# Revit family: HermanMiller_Seating_Aeron_WorkChair
name_source: partatom
category: Furniture
revit_build: Autodesk Revit Architecture 2012 (Build: 20110622_0930(x64)
units: mm (PartAtom-declared; Revit-internal decimal feet)

## types (12) — shared parameters
Assembly Code = E2020200
Catalog = Seating (HST)
Manufacturer = Herman Miller, Inc.
Product Documentation Link = http://www.hermanmiller.com
Type Comments = Aeron Work Chair - AE11 Series
URL = http://www.hermanmiller.com

## per-type parameters (varying)
| type | Arm On | Armpad Finish | Base Finish | Description | Frame Finish | Lumbar Finish | Lumbar Support | Model | PostureFit Finish | PostureFit support | Seat Material |
| Arms No Back Support - Graphite Base/Graphite Frame | Yes | Herman Miller - Finish BK Black | Herman Miller - Finish G1 Graphite | Wk Chr Aeron Std-Ht Pneu Tlt Lim/Ang Ht Adj Arms NonuphstPds/B | Herman Miller - Finish G1 Graphite | Herman Miller - Finish BK Black | No | AE113HWB N2 G1 | Herman Miller - Finish G1 Graphite | No | Herman Miller - Pellicle 3D01 Classic Carbon |
| Arms No Back Support - Titanium Base/Smoke Frame | Yes | Herman Miller - Finish S8 Smoke | Herman Miller - Finish XT Titanium | Wk Chr Aeron Std-Ht Pneu Tlt Lim/Ang Ht Adj Arms NonuphstPds/B | Herman Miller - Finish S8 Smoke | Herman Miller - Finish S8 Smoke | No | AE113HWB N2 WS | Herman Miller - Finish S8 Smoke | No | Herman Miller - Pellicle 3V01 Classic Zinc |
| Arms Lumbar Support - Graphite Base/Graphite Frame | Yes | Herman Miller - Finish BK Black | Herman Miller - Finish G1 Graphite | Wk Chr Aeron Std-Ht Pneu Tlt Lim/Ang Ht Adj Arms NonuphstPds/B | Herman Miller - Finish G1 Graphite | Herman Miller - Finish BK Black | Yes | AE113HWB AJ G1 | Herman Miller - Finish G1 Graphite | No | Herman Miller - Pellicle 3D01 Classic Carbon |
| Arms Lumbar Support - Titanium Base/Smoke Frame | Yes | Herman Miller - Finish S8 Smoke | Herman Miller - Finish XT Titanium | Wk Chr Aeron Std-Ht Pneu Tlt Lim/Ang Ht Adj Arms NonuphstPds/B | Herman Miller - Finish S8 Smoke | Herman Miller - Finish S8 Smoke | Yes | AE113HWB AJ WS | Herman Miller - Finish S8 Smoke | No | Herman Miller - Pellicle 3V01 Classic Zinc |
| Arms PostureFit Support - Graphite Base/Graphite Frame | Yes | Herman Miller - Finish BK Black | Herman Miller - Finish G1 Graphite | Wk Chr Aeron Std-Ht Pneu Tlt Lim/Ang Ht Adj Arms NonuphstPds/B | Herman Miller - Finish G1 Graphite | Herman Miller - Finish BK Black | No | AE113HWB PJ G1 | Herman Miller - Finish G1 Graphite | Yes | Herman Miller - Pellicle 3D01 Classic Carbon |
| Arms PostureFit Support - Titanium Base/Smoke Frame | Yes | Herman Miller - Finish S8 Smoke | Herman Miller - Finish XT Titanium | Wk Chr Aeron Std-Ht Pneu Tlt Lim/Ang Ht Adj Arms NonuphstPds/B | Herman Miller - Finish S8 Smoke | Herman Miller - Finish S8 Smoke | No | AE113HWB PJ WS | Herman Miller - Finish S8 Smoke | Yes | Herman Miller - Pellicle 3V01 Classic Zinc |
| Without Arms No Back Support - Graphite Base/Graphite Frame | No | Herman Miller - Finish BK Black | Herman Miller - Finish G1 Graphite | Wk Chr Aeron Std-Ht Pneu. Tlt Lim/Ang No Arms/B | Herman Miller - Finish G1 Graphite | Herman Miller - Finish BK Black | No | AE113NNB N2 G1 | Herman Miller - Finish G1 Graphite | No | Herman Miller - Pellicle 3D01 Classic Carbon |
| Without Arms No Back Support - Titanium Base/Smoke Frame | No | Herman Miller - Finish S8 Smoke | Herman Miller - Finish XT Titanium | Wk Chr Aeron Std-Ht Pneu. Tlt Lim/Ang No Arms/B | Herman Miller - Finish S8 Smoke | Herman Miller - Finish S8 Smoke | No | AE113NNB N2 WS | Herman Miller - Finish S8 Smoke | No | Herman Miller - Pellicle 3V01 Classic Zinc |
| Without Arms Lumbar Support - Graphite Base/Graphite Frame | No | Herman Miller - Finish BK Black | Herman Miller - Finish G1 Graphite | Wk Chr Aeron Std-Ht Pneu. Tlt Lim/Ang No Arms/B | Herman Miller - Finish G1 Graphite | Herman Miller - Finish BK Black | Yes | AE113NNB AJ G1 | Herman Miller - Finish G1 Graphite | No | Herman Miller - Pellicle 3D01 Classic Carbon |
| Without Arms Lumbar Support - Titanium Base/Smoke Frame | No | Herman Miller - Finish S8 Smoke | Herman Miller - Finish XT Titanium | Wk Chr Aeron Std-Ht Pneu. Tlt Lim/Ang No Arms/B | Herman Miller - Finish S8 Smoke | Herman Miller - Finish S8 Smoke | Yes | AE113NNB AJ WS | Herman Miller - Finish S8 Smoke | No | Herman Miller - Pellicle 3V01 Classic Zinc |
| Without Arms PostureFit Support - Graphite Base/Graphite Frame | No | Herman Miller - Finish BK Black | Herman Miller - Finish G1 Graphite | Wk Chr Aeron Std-Ht Pneu. Tlt Lim/Ang No Arms/B | Herman Miller - Finish G1 Graphite | Herman Miller - Finish BK Black | No | AE113NNB PJ G1 | Herman Miller - Finish G1 Graphite | Yes | Herman Miller - Pellicle 3D01 Classic Carbon |
| Without Arms PostureFit Support - Titanium Base/Smoke Frame | No | Herman Miller - Finish S8 Smoke | Herman Miller - Finish XT Titanium | Wk Chr Aeron Std-Ht Pneu. Tlt Lim/Ang No Arms/B | Herman Miller - Finish S8 Smoke | Herman Miller - Finish S8 Smoke | No | AE113NNB PJ WS | Herman Miller - Finish S8 Smoke | Yes | Herman Miller - Pellicle 3V01 Classic Zinc |

## geometry (parser evidence)
native form markers: Blend x20, Sweep x2
no freeform markers — native parametric forms only
